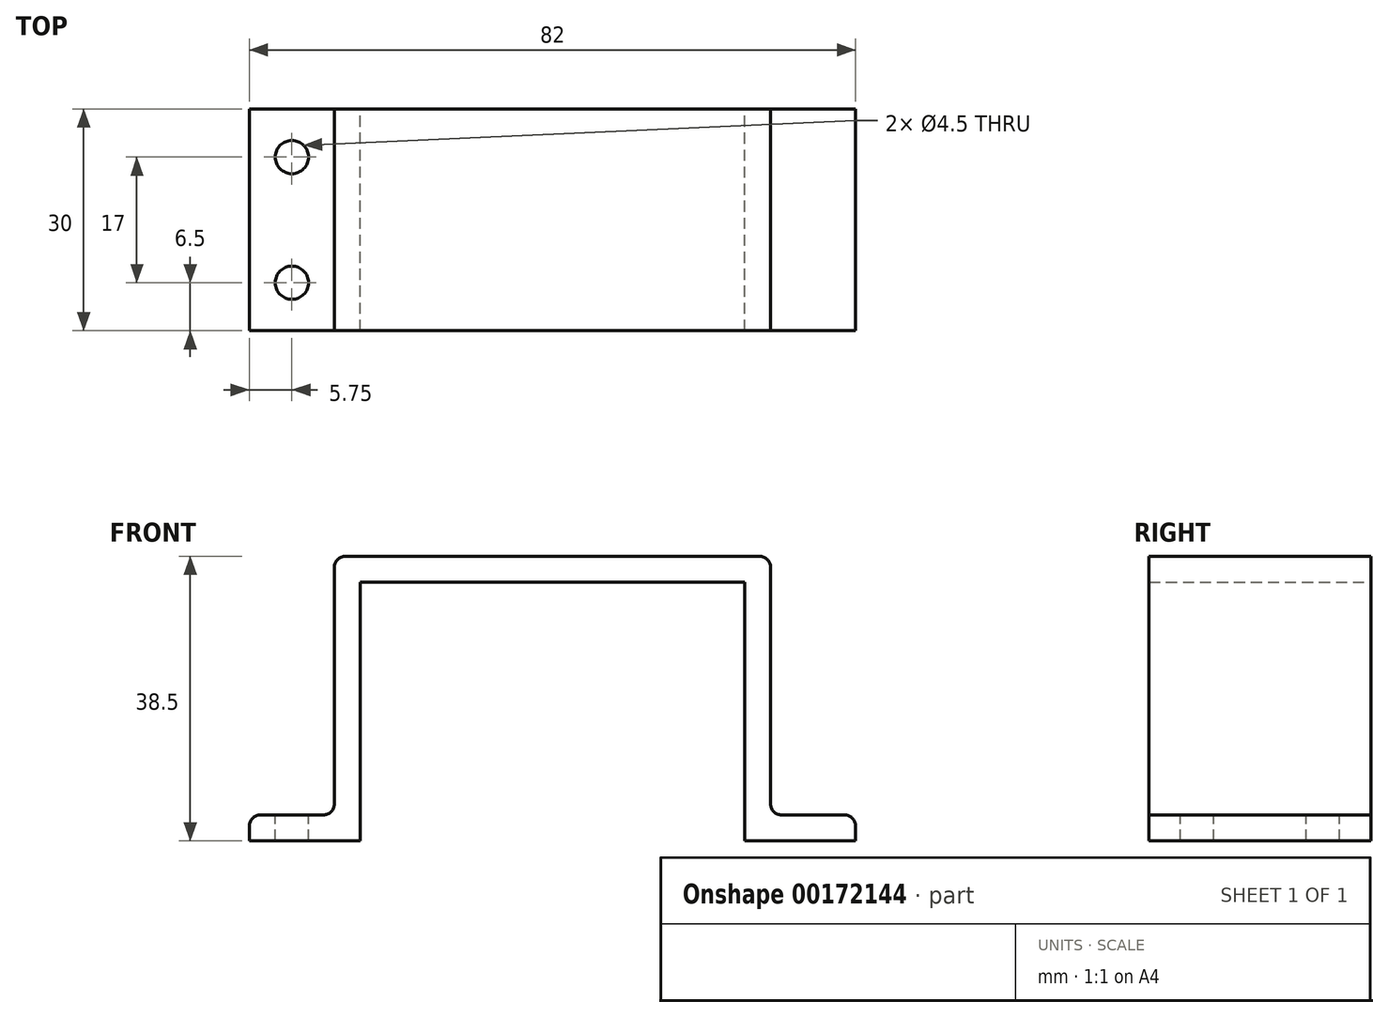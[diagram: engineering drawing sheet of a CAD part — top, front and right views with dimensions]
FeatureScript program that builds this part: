
annotation { "Feature Type Name" : "Feature", "Feature Type Description" : "" }
export const myFeature = defineFeature(function(context is Context, id is Id, definition is map)
    precondition{}
    {
        {
            var Q0;
            Q0=qCreatedBy(makeId("Front.planeOp"),FACE);
            var sketch = newSketch(context, id + "F0", { "sketchPlane" : qUnion([Q0])});
            skLineSegment(sketch, "E0.top", {"start": v(-26, 31.5) * mm, "end": v(26, 31.5) * mm});
            skLineSegment(sketch, "E0.left", {"start": v(-26, 0) * mm, "end": v(-26, 31.5) * mm});
            skLineSegment(sketch, "E0.right", {"start": v(26, 0) * mm, "end": v(26, 31.5) * mm});
            skLineSegment(sketch, "E1.bottom", {"start": v(-29.5, 0) * mm, "end": v(-26, 0) * mm});
            skLineSegment(sketch, "E1.top", {"start": v(-29.5, 35) * mm, "end": v(29.5, 35) * mm});
            skLineSegment(sketch, "E1.left", {"start": v(-29.5, 0) * mm, "end": v(-29.5, 35) * mm});
            skLineSegment(sketch, "E1.right", {"start": v(29.5, 0) * mm, "end": v(29.5, 35) * mm});
            skLineSegment(sketch, "E2.bottom", {"start": v(-41, 0) * mm, "end": v(-29.5, 0) * mm});
            skLineSegment(sketch, "E2.top", {"start": v(-41, -3.5) * mm, "end": v(-26, -3.5) * mm});
            skLineSegment(sketch, "E2.left", {"start": v(-41, 0) * mm, "end": v(-41, -3.5) * mm});
            skLineSegment(sketch, "E2.right", {"start": v(41, 0) * mm, "end": v(41, -3.5) * mm});
            skPoint(sketch, "E3", {"position": v(0, -3.5) * mm});
            skLineSegment(sketch, "E4", {"start": v(-26, 0) * mm, "end": v(-26, -3.5) * mm});
            skLineSegment(sketch, "E5", {"start": v(26, 0) * mm, "end": v(26, -3.5) * mm});
            skLineSegment(sketch, "E6.trimOffspring", {"start": v(26, 0) * mm, "end": v(41, 0) * mm});
            skLineSegment(sketch, "E7.trimOffspring", {"start": v(26, -3.5) * mm, "end": v(41, -3.5) * mm});
            skSolve(sketch);
        }
        {
            var Q0;
            Q0 = qSketchRegion(id + "F0", true);
            extrude(context, id + "F1", {"entities" : qUnion([Q0]), "depth" : 30 * mm});
        }
        {
            var Q0;
            Q0=makeQuery(id+"F1.opExtrude","SWEPT_FACE",FACE,{"disambiguationData":[OSD([sQuery(id+"F0.wireOp",EDGE,"E2.bottom")])]});
            var sketch = newSketch(context, id + "F2", { "sketchPlane" : qUnion([Q0])});
            skLineSegment(sketch, "E8", {"start": v(-35.25, 0) * mm, "end": v(-35.25, -30) * mm, "construction": true});
            skCircle(sketch, "E9", {"center": v(-35.25, -23.5) * mm, "radius": 2.25 * mm});
            skLineSegment(sketch, "E10", {"start": v(-41, -15) * mm, "end": v(-29.5, -15) * mm, "construction": true});
            skCircle(sketch, "E11.MirrorC", {"center": v(-35.25, -6.5) * mm, "radius": 2.25 * mm});
            skSolve(sketch);
        }
        {
            var Q0;
            Q0 = qSketchRegion(id + "F2", true);
            var Q1;
            Q1=makeQuery(id+"F1.opExtrude","SWEPT_FACE",FACE,{"disambiguationData":[OSD([sQuery(id+"F0.wireOp",EDGE,"E2.top")])]});
            extrude(context, id + "F3", {"entities" : qUnion([Q0]), "operationType" : NewBodyOperationType.REMOVE, "endBound" : BoundingType.UP_TO_SURFACE, "oppositeDirection" : true, "endBoundEntityFace" : qUnion([Q1]), "depth" : 25 * mm});
        }
        {
            var Q0;
            Q0=makeQuery(id+"F1.opExtrude","SWEPT_EDGE",EDGE,{"disambiguationData":[OSD([sQuery(id+"F0.wireOp",EDGE,"E1.top"),sQuery(id+"F0.wireOp",EDGE,"E1.left")])]});
            var Q1;
            Q1=makeQuery(id+"F1.opExtrude","SWEPT_EDGE",EDGE,{"disambiguationData":[OSD([sQuery(id+"F0.wireOp",EDGE,"E1.bottom"),sQuery(id+"F0.wireOp",EDGE,"E1.left"),sQuery(id+"F0.wireOp",EDGE,"E2.bottom")])]});
            var Q2;
            Q2=makeQuery(id+"F1.opExtrude","SWEPT_EDGE",EDGE,{"disambiguationData":[OSD([sQuery(id+"F0.wireOp",EDGE,"E2.bottom"),sQuery(id+"F0.wireOp",EDGE,"E2.left")])]});
            var Q3;
            Q3=makeQuery(id+"F1.opExtrude","SWEPT_EDGE",EDGE,{"disambiguationData":[OSD([sQuery(id+"F0.wireOp",EDGE,"E1.top"),sQuery(id+"F0.wireOp",EDGE,"E1.right")])]});
            var Q4;
            Q4=makeQuery(id+"F1.opExtrude","SWEPT_EDGE",EDGE,{"disambiguationData":[OSD([sQuery(id+"F0.wireOp",EDGE,"E1.right"),sQuery(id+"F0.wireOp",EDGE,"E6.trimOffspring")])]});
            var Q5;
            Q5=makeQuery(id+"F1.opExtrude","SWEPT_EDGE",EDGE,{"disambiguationData":[OSD([sQuery(id+"F0.wireOp",EDGE,"E2.right"),sQuery(id+"F0.wireOp",EDGE,"E6.trimOffspring")])]});
            fillet(context, id + "F4", {"entities" : qUnion([Q0, Q1, Q2, Q3, Q4, Q5]), "radius" : 1.5 * mm, "tangentPropagation" : true, "allowEdgeOverflow" : false});
        }
    });
